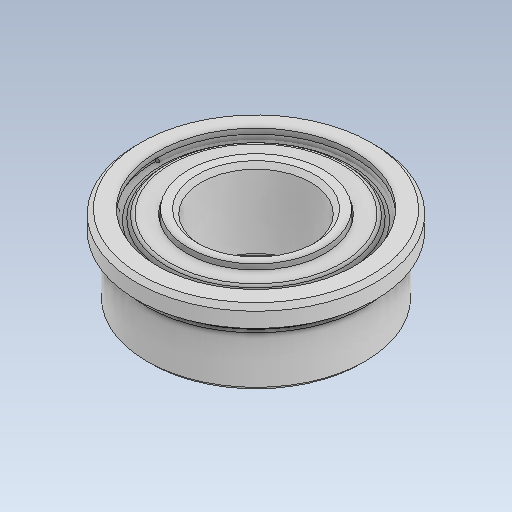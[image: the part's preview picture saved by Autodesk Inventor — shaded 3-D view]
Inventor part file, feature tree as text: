
AUTODESK INVENTOR PART (.ipt)
format: ipt  version: 2020 (Build 240168000, 168)  size: 271,360 bytes
history: native  units: in
note: dims shown in document units (in); Inventor stores cm internally (conversion verified against a paired STEP export)
features: revolve x1, fillet x1, mirror x1
ambient origin geometry x8: Origin, YZ Plane, XZ Plane, XY Plane, X Axis, Y Axis, Z Axis, Center Point
bodies: Solid1 (feature_tree), Solid2 (feature_tree), Solid3 (feature_tree)
feature tree (3):
  revolve  "Revolve1"  [1 undecoded]
  fillet  "Fillet1"  [1 undecoded]
  mirror  "Mirror8"
note: 2 required parameter values undecoded (feature->parameter linkage not recoverable at this tier; creation-order binding heuristic only, values carry confidence <= 0.55)
